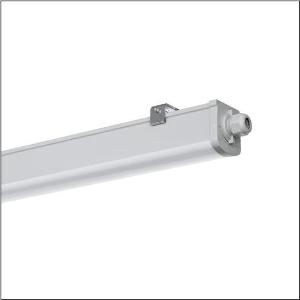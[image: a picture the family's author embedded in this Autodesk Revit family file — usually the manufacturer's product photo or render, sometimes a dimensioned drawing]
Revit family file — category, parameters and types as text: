
# Revit family: monsun_r__31_51fa20dd420b_de40
name_source: partatom
category: Lighting Fixtures
units: mm (PartAtom-declared; Revit-internal decimal feet)

## family parameters
Cut with Voids When Loaded = No
Host = Face
Light Source = No
Part Type = Normal
Room Calculation Point = No
Round Connector Dimension = Use Diameter
Shared = No

## types (1)
- Monsun® 31 (1 x LED, 2300 lm, 19 W, 4000K)
    Apparent Load = 19 VA
    CIE Flux Codes = 42 72 91 92 100
    Color Rendering = 80
    Color Temperature = 4000K
    Default Elevation = 1800 mm
    Description = Monsun® 31, damp-proof luminaire, primary optical cover: diffuser, of PC, frosted, light emission: direct distribution, primary light characteristic: symmetric, installation type: surface-mounted, LED, rated luminous flux: 2.300lm, luminous efficacy: 121lm/W, light colour: 840, colour temperature: 4000K, control gear: ECG, with terminal, 5+1-pole, max. 2.5mm², through-wiring: 3x 2.5mm² + 3x 1.5mm², mains connection: 220..240V, AC, 50/60Hz, rated input power: 19W, housing, luminaire housing, of PC, light grey (RAL 7035), length: 558mm, width: 68mm, height: 76mm, protection rating (complete): IP66, insulation class (complete): insulation class II (safety insulation), certification: CE, ENEC, UKCA, protection symbol: D, impact resistance: IK08, permissible operating ambient temperature: -20..+40°C, corresponds to IFS (International Featured Standards) requirements for safety and quality in the food industry, contact your sales advisor before using the luminaires in applications with unclear chemical exposure, large temperature fluctuations or condensation-forming humidity, packaging unit: 1 piece
    Height = 77 mm
    Lamp = 1 x LED
    Lamp Light Flux = 2300 lm
    Lamp Power = 19 W
    Lamp count = 1
    Length = 618 mm
    Luminous efficacy = 121 lm/W
    Manufacturer = Siteco
    ModVariant = No
    Model = 51FA20DD420B
    Mounting Place = Ceiling
    Mounting Type = Surface mounted
    Number of Poles = 1
    OnlyDefault = Yes
    Power Factor = 1
    Product Name = Monsun® 31
    Product group = damp-proof luminaire
    ProductGroupID = 300
    Protection Class = Protection class II
    Protection Degree = IP 66
    RLX_Detail_Level = 1
    RLX_Emergency_Light_Flux = 0 lm
    RLX_Emergency_Type = 0
    RLX_Emergency_Type_DB = No
    RlxData = <blob elided: 32985 chars, md5=85e2075b>
    Socket = socket
    Standby Power = 0 W
    System Light Flux = 2300 lm
    System Power = 19 W
    Type Comments = Product without accessories
    Type Image = l_1006174.jpg
    URL = http://relux.com
    VarID = ---
    Voltage = 0 V
    Weight = 0.00 kg
    Width = 69 mm

## geometry (parser evidence)
native form markers: Blend x4, Sweep x13
no freeform markers — native parametric forms only
